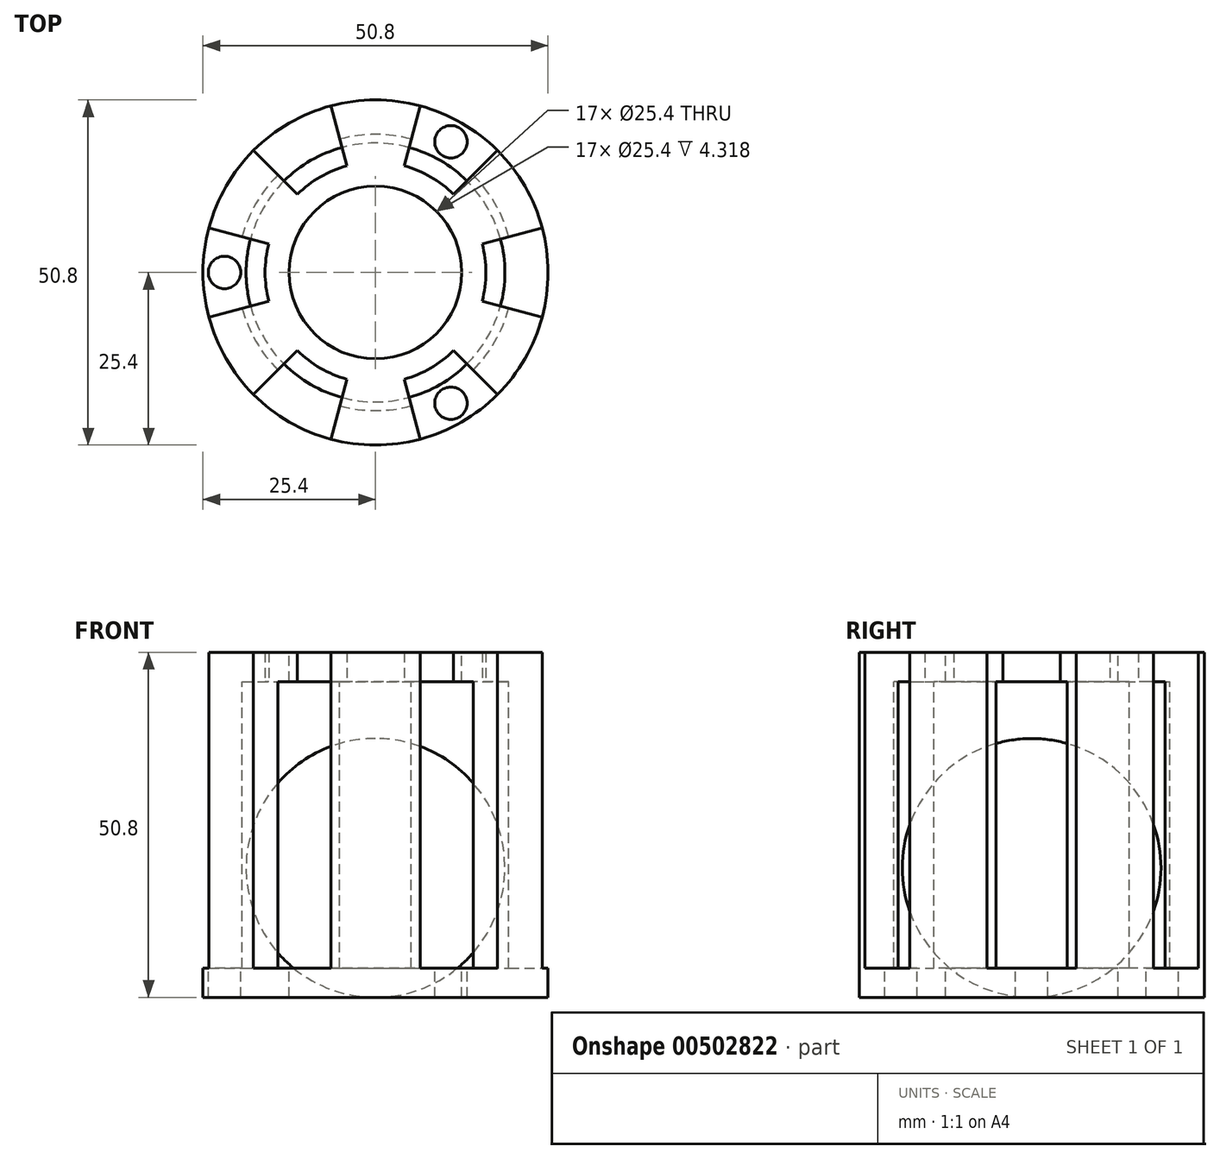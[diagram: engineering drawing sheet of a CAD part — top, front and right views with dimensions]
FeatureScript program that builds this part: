
annotation { "Feature Type Name" : "Feature", "Feature Type Description" : "" }
export const myFeature = defineFeature(function(context is Context, id is Id, definition is map)
    precondition{}
    {
        {
            var Q0;
            Q0=qCreatedBy(makeId("Top.planeOp"),FACE);
            var sketch = newSketch(context, id + "F0", { "sketchPlane" : qUnion([Q0])});
            skCircle(sketch, "E0", {"center": v(0, 0) * mm, "radius": 25.4 * mm});
            skSolve(sketch);
        }
        {
            var Q0;
            Q0=makeQuery(id+"F0.imprint","IMPRINT",FACE,{"disambiguationData":[TD([[makeQuery(id+"F0.imprint","IMPRINT",EDGE,{"derivedFrom":sQuery(id+"F0.wireOp",EDGE,"E0")}),1.0]])]});
            extrude(context, id + "F1", {"entities" : qUnion([Q0]), "endBound" : BoundingType.SYMMETRIC, "depth" : 50.8 * mm});
        }
        {
            var Q0;
            Q0=qCreatedBy(makeId("Top.planeOp"),FACE);
            var sketch = newSketch(context, id + "F2", { "sketchPlane" : qUnion([Q0])});
            skCircle(sketch, "E1", {"center": v(0, 0) * mm, "radius": 12.7 * mm});
            skSolve(sketch);
        }
        {
            var Q0;
            Q0 = qSketchRegion(id + "F2", true);
            extrude(context, id + "F3", {"entities" : qUnion([Q0]), "operationType" : NewBodyOperationType.REMOVE, "endBound" : BoundingType.THROUGH_ALL, "oppositeDirection" : true, "depth" : 25.4 * mm, "hasSecondDirection" : true, "secondDirectionBound" : SecondDirectionBoundingType.THROUGH_ALL, "secondDirectionOppositeDirection" : false, "secondDirectionDepth" : 25.4 * mm});
        }
        {
            var Q0;
            Q0=qCreatedBy(makeId("Top.planeOp"),FACE);
            var sketch = newSketch(context, id + "F4", { "sketchPlane" : qUnion([Q0])});
            skCircle(sketch, "E2", {"center": v(0, 0) * mm, "radius": 20.32 * mm});
            skSolve(sketch);
        }
        {
            var Q0;
            Q0 = qSketchRegion(id + "F4", true);
            extrude(context, id + "F5", {"entities" : qUnion([Q0]), "operationType" : NewBodyOperationType.REMOVE, "endBound" : BoundingType.SYMMETRIC, "oppositeDirection" : true, "depth" : 42.16 * mm});
        }
        {
            var Q0;
            Q0=qCreatedBy(makeId("Top.planeOp"),FACE);
            var sketch = newSketch(context, id + "F6", { "sketchPlane" : qUnion([Q0])});
            skCircle(sketch, "E3", {"center": v(0, 0) * mm, "radius": 22.23 * mm, "construction": true});
            skCircle(sketch, "E4", {"center": v(-22.23, 0) * mm, "radius": 2.39 * mm});
            skCircle(sketch, "E5", {"center": v(11.11, 19.25) * mm, "radius": 2.39 * mm});
            skCircle(sketch, "E6", {"center": v(11.11, -19.25) * mm, "radius": 2.39 * mm});
            skLineSegment(sketch, "E7", {"start": v(0, 0) * mm, "end": v(11.11, 19.25) * mm, "construction": true});
            skLineSegment(sketch, "E8", {"start": v(0, 0) * mm, "end": v(11.11, -19.25) * mm, "construction": true});
            skLineSegment(sketch, "E9", {"start": v(-22.23, 0) * mm, "end": v(22.23, 0) * mm, "construction": true});
            skSolve(sketch);
        }
        {
            var Q0;
            Q0 = qSketchRegion(id + "F6", true);
            var Q1;
            Q1=makeQuery(id+"F5.boolean.opBoolean","COPY",FACE,{"derivedFrom":makeQuery(id+"F5.opExtrude","CAP_FACE",FACE,{"disambiguationData":[OSD([sQuery(id+"F4.wireOp",EDGE,"E2")])],"isStart":false})});
            extrude(context, id + "F7", {"entities" : qUnion([Q0]), "operationType" : NewBodyOperationType.REMOVE, "endBound" : BoundingType.THROUGH_ALL, "oppositeDirection" : true, "depth" : 25.4 * mm, "hasSecondDirection" : true, "secondDirectionBound" : SecondDirectionBoundingType.THROUGH_ALL, "secondDirectionOppositeDirection" : false, "secondDirectionBoundEntityFace" : qUnion([Q1]), "secondDirectionDepth" : 25.4 * mm});
        }
        {
            var Q0;
            Q0=qCreatedBy(makeId("Top.planeOp"),FACE);
            var sketch = newSketch(context, id + "F8", { "sketchPlane" : qUnion([Q0])});
            skLineSegment(sketch, "E10", {"start": v(-24.53, 6.57) * mm, "end": v(-15.7, 4.2) * mm});
            skLineSegment(sketch, "E11", {"start": v(-15.7, -4.2) * mm, "end": v(-24.53, -6.57) * mm});
            skLineSegment(sketch, "E12", {"start": v(0, 0) * mm, "end": v(-25.69, 0) * mm, "construction": true});
            skArc(sketch, "E13", {"start": v(-24.53, 6.57) * mm, "mid": v(-25.4, 0) * mm, "end": v(-24.53, -6.57) * mm});
            skArc(sketch, "E14", {"start": v(-15.7, 4.2) * mm, "mid": v(-16.26, 0) * mm, "end": v(-15.7, -4.2) * mm});
            skLineSegment(sketch, "E15", {"start": v(0, 0) * mm, "end": v(-22, 12.7) * mm, "construction": true});
            skArc(sketch, "E16.MirrorCS", {"start": v(-17.96, 17.96) * mm, "mid": v(-12.7, 22) * mm, "end": v(-6.57, 24.53) * mm});
            skLineSegment(sketch, "E17.MirrorCS", {"start": v(-17.96, 17.96) * mm, "end": v(-11.5, 11.5) * mm});
            skArc(sketch, "E18.MirrorCS", {"start": v(-11.5, 11.5) * mm, "mid": v(-8.13, 14.08) * mm, "end": v(-4.2, 15.7) * mm});
            skLineSegment(sketch, "E19.MirrorCS", {"start": v(-4.2, 15.7) * mm, "end": v(-6.57, 24.53) * mm});
            skArc(sketch, "E20.MirrorCS", {"start": v(-17.96, -17.96) * mm, "mid": v(-12.7, -22) * mm, "end": v(-6.57, -24.53) * mm});
            skLineSegment(sketch, "E21.MirrorCS", {"start": v(-17.96, -17.96) * mm, "end": v(-11.5, -11.5) * mm});
            skArc(sketch, "E22.MirrorCS", {"start": v(-11.5, -11.5) * mm, "mid": v(-8.13, -14.08) * mm, "end": v(-4.2, -15.7) * mm});
            skLineSegment(sketch, "E23.MirrorCS", {"start": v(-4.2, -15.7) * mm, "end": v(-6.57, -24.53) * mm});
            skLineSegment(sketch, "E24", {"start": v(0, 25.36) * mm, "end": v(0, -25.53) * mm, "construction": true});
            skArc(sketch, "E25.MirrorCS", {"start": v(17.96, 17.96) * mm, "mid": v(12.7, 22) * mm, "end": v(6.57, 24.53) * mm});
            skLineSegment(sketch, "E26.MirrorCS", {"start": v(4.2, 15.7) * mm, "end": v(6.57, 24.53) * mm});
            skArc(sketch, "E27.MirrorCS", {"start": v(11.5, 11.5) * mm, "mid": v(8.13, 14.08) * mm, "end": v(4.2, 15.7) * mm});
            skLineSegment(sketch, "E28.MirrorCS", {"start": v(17.96, 17.96) * mm, "end": v(11.5, 11.5) * mm});
            skLineSegment(sketch, "E29.MirrorCS", {"start": v(24.53, 6.57) * mm, "end": v(15.7, 4.2) * mm});
            skLineSegment(sketch, "E30.MirrorCS", {"start": v(15.7, -4.2) * mm, "end": v(24.53, -6.57) * mm});
            skArc(sketch, "E31.MirrorCS", {"start": v(11.5, -11.5) * mm, "mid": v(8.13, -14.08) * mm, "end": v(4.2, -15.7) * mm});
            skLineSegment(sketch, "E32.MirrorCS", {"start": v(4.2, -15.7) * mm, "end": v(6.57, -24.53) * mm});
            skLineSegment(sketch, "E33.MirrorCS", {"start": v(17.96, -17.96) * mm, "end": v(11.5, -11.5) * mm});
            skArc(sketch, "E34.MirrorCS", {"start": v(17.96, -17.96) * mm, "mid": v(12.7, -22) * mm, "end": v(6.57, -24.53) * mm});
            skArc(sketch, "E35", {"start": v(15.7, 4.2) * mm, "mid": v(16.26, 0) * mm, "end": v(15.7, -4.2) * mm});
            skArc(sketch, "E36", {"start": v(24.53, 6.57) * mm, "mid": v(25.4, 0) * mm, "end": v(24.53, -6.57) * mm});
            skSolve(sketch);
        }
        {
            var Q0;
            Q0 = qSketchRegion(id + "F8", true);
            var Q1;
            Q1=makeQuery(id+"F5.boolean.opBoolean","COPY",FACE,{"derivedFrom":makeQuery(id+"F5.opExtrude","CAP_FACE",FACE,{"disambiguationData":[OSD([sQuery(id+"F4.wireOp",EDGE,"E2")])],"isStart":false})});
            extrude(context, id + "F9", {"entities" : qUnion([Q0]), "operationType" : NewBodyOperationType.REMOVE, "endBound" : BoundingType.THROUGH_ALL, "depth" : 25.4 * mm, "hasSecondDirection" : true, "secondDirectionBound" : SecondDirectionBoundingType.UP_TO_SURFACE, "secondDirectionOppositeDirection" : true, "secondDirectionBoundEntityFace" : qUnion([Q1]), "secondDirectionDepth" : 25.4 * mm});
        }
        {
            var Q0;
            Q0=qCreatedBy(makeId("Front.planeOp"),FACE);
            var sketch = newSketch(context, id + "F10", { "sketchPlane" : qUnion([Q0])});
            skLineSegment(sketch, "E37", {"start": v(0, 25.54) * mm, "end": v(0, -25.8) * mm, "construction": true});
            skArc(sketch, "E38", {"start": v(0, 12.7) * mm, "mid": v(19.05, -6.35) * mm, "end": v(0, -25.4) * mm});
            skLineSegment(sketch, "E39", {"start": v(0, 12.7) * mm, "end": v(0, -25.4) * mm});
            skSolve(sketch);
        }
        {
            var Q0;
            Q0 = qSketchRegion(id + "F10", true);
            var Q1;
            Q1=sQuery(id+"F10.wireOp",EDGE,"E37");
            revolve(context, id + "F11", {"entities" : qUnion([Q0]), "axis" : qUnion([Q1]), "revolveType" : RevolveType.FULL});
        }
    });
